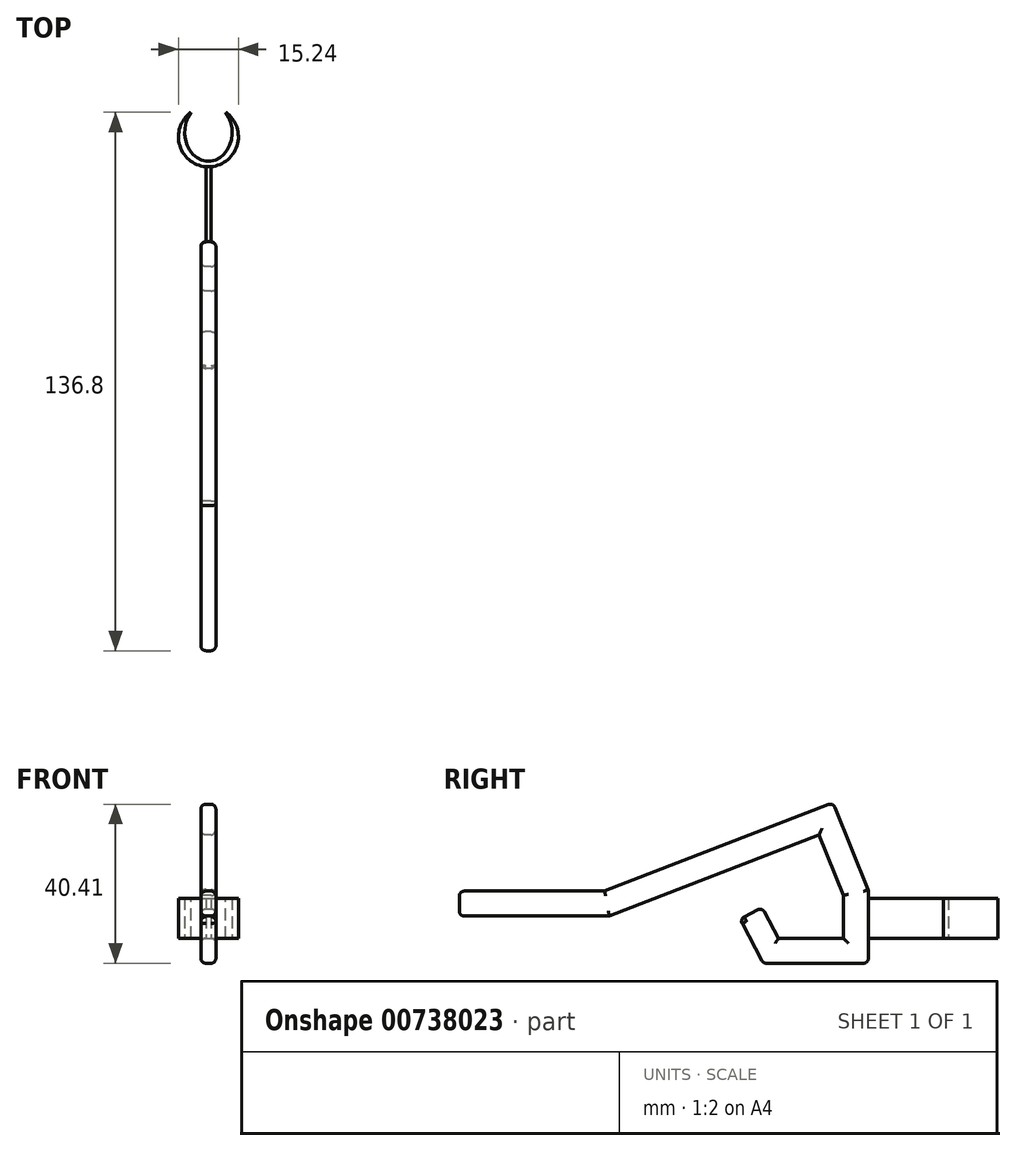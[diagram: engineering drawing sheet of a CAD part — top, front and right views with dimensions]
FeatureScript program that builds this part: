
annotation { "Feature Type Name" : "Feature", "Feature Type Description" : "" }
export const myFeature = defineFeature(function(context is Context, id is Id, definition is map)
    precondition{}
    {
        {
            var Q0;
            Q0=qCreatedBy(makeId("Right.planeOp"),FACE);
            var sketch = newSketch(context, id + "F0", { "sketchPlane" : qUnion([Q0])});
            skLineSegment(sketch, "E0", {"start": v(0, 0) * mm, "end": v(38.1, 0) * mm});
            skLineSegment(sketch, "E1", {"start": v(38.1, 0) * mm, "end": v(67.72, 11.44) * mm});
            skLineSegment(sketch, "E2", {"start": v(67.72, 11.44) * mm, "end": v(91.4, 20.6) * mm});
            skLineSegment(sketch, "E3", {"start": v(91.4, 20.6) * mm, "end": v(97.57, 5.28) * mm});
            skLineSegment(sketch, "E4", {"start": v(97.57, 5.28) * mm, "end": v(97.57, -5.65) * mm});
            skLineSegment(sketch, "E5", {"start": v(97.57, -5.65) * mm, "end": v(81.06, -5.65) * mm});
            skLineSegment(sketch, "E6", {"start": v(81.06, -5.65) * mm, "end": v(76.88, 2.2) * mm});
            skLineSegment(sketch, "E7", {"start": v(76.88, 2.2) * mm, "end": v(71.27, -0.8) * mm});
            skLineSegment(sketch, "E8", {"start": v(94.96, 28.78) * mm, "end": v(67.72, 18.25) * mm});
            skLineSegment(sketch, "E9", {"start": v(67.72, 18.25) * mm, "end": v(36.92, 6.35) * mm});
            skLineSegment(sketch, "E10", {"start": v(36.92, 6.35) * mm, "end": v(0, 6.35) * mm});
            skLineSegment(sketch, "E11", {"start": v(0, 6.35) * mm, "end": v(0, 0) * mm});
            skLineSegment(sketch, "E12", {"start": v(94.96, 28.78) * mm, "end": v(103.92, 6.5) * mm});
            skLineSegment(sketch, "E13", {"start": v(71.27, -0.8) * mm, "end": v(77.25, -12) * mm});
            skLineSegment(sketch, "E14", {"start": v(103.92, 6.5) * mm, "end": v(103.92, -12) * mm});
            skLineSegment(sketch, "E15", {"start": v(103.92, -12) * mm, "end": v(77.25, -12) * mm});
            skSolve(sketch);
        }
        {
            var Q0;
            Q0 = qSketchRegion(id + "F0", true);
            extrude(context, id + "F1", {"entities" : qUnion([Q0]), "depth" : 3.8 * mm, "offsetDistance" : 25.4 * mm});
        }
        {
            var Q0;
            Q0=makeQuery(id+"F1.opExtrude","SWEPT_EDGE",EDGE,{"disambiguationData":[OSD([sQuery(id+"F0.wireOp",EDGE,"E10"),sQuery(id+"F0.wireOp",EDGE,"E11")])]});
            var Q1;
            Q1=makeQuery(id+"F1.opExtrude","SWEPT_EDGE",EDGE,{"disambiguationData":[OSD([sQuery(id+"F0.wireOp",EDGE,"E0"),sQuery(id+"F0.wireOp",EDGE,"E11")])]});
            var Q2;
            Q2=makeQuery(id+"F1.opExtrude","CAP_EDGE",EDGE,{"disambiguationData":[OSD([sQuery(id+"F0.wireOp",EDGE,"E11")])],"isStart":false});
            var Q3;
            Q3=makeQuery(id+"F1.opExtrude","CAP_EDGE",EDGE,{"disambiguationData":[OSD([sQuery(id+"F0.wireOp",EDGE,"E0")])],"isStart":false});
            var Q4;
            Q4=makeQuery(id+"F1.opExtrude","CAP_EDGE",EDGE,{"disambiguationData":[OSD([sQuery(id+"F0.wireOp",EDGE,"E10")])],"isStart":false});
            var Q5;
            Q5=makeQuery(id+"F1.opExtrude","CAP_EDGE",EDGE,{"disambiguationData":[OSD([sQuery(id+"F0.wireOp",EDGE,"E0")])],"isStart":true});
            var Q6;
            Q6=makeQuery(id+"F1.opExtrude","CAP_EDGE",EDGE,{"disambiguationData":[OSD([sQuery(id+"F0.wireOp",EDGE,"E10")])],"isStart":true});
            var Q7;
            Q7=makeQuery(id+"F1.opExtrude","CAP_EDGE",EDGE,{"disambiguationData":[OSD([sQuery(id+"F0.wireOp",EDGE,"E9")])],"isStart":true});
            var Q8;
            Q8=makeQuery(id+"F1.opExtrude","CAP_EDGE",EDGE,{"disambiguationData":[OSD([sQuery(id+"F0.wireOp",EDGE,"E9")])],"isStart":false});
            var Q9;
            Q9=makeQuery(id+"F1.opExtrude","CAP_EDGE",EDGE,{"disambiguationData":[OSD([sQuery(id+"F0.wireOp",EDGE,"E1")])],"isStart":false});
            var Q10;
            Q10=makeQuery(id+"F1.opExtrude","CAP_EDGE",EDGE,{"disambiguationData":[OSD([sQuery(id+"F0.wireOp",EDGE,"E1")])],"isStart":true});
            var Q11;
            Q11=makeQuery(id+"F1.opExtrude","CAP_EDGE",EDGE,{"disambiguationData":[OSD([sQuery(id+"F0.wireOp",EDGE,"E11")])],"isStart":true});
            fillet(context, id + "F2", {"entities" : qUnion([Q0, Q1, Q2, Q3, Q4, Q5, Q6, Q7, Q8, Q9, Q10, Q11]), "radius" : 1.27 * mm, "tangentPropagation" : true, "allowEdgeOverflow" : false});
        }
        {
            var Q0;
            Q0=makeQuery(id+"F1.opExtrude","CAP_EDGE",EDGE,{"disambiguationData":[OSD([sQuery(id+"F0.wireOp",EDGE,"E8")])],"isStart":false});
            var Q1;
            Q1=makeQuery(id+"F1.opExtrude","CAP_EDGE",EDGE,{"disambiguationData":[OSD([sQuery(id+"F0.wireOp",EDGE,"E8")])],"isStart":true});
            var Q2;
            Q2=makeQuery(id+"F1.opExtrude","CAP_EDGE",EDGE,{"disambiguationData":[OSD([sQuery(id+"F0.wireOp",EDGE,"q7BT2R1Q-RqXa-ez77-BYZs-truSc1ktzAL2")])],"isStart":false});
            var Q3;
            Q3=makeQuery(id+"F1.opExtrude","CAP_EDGE",EDGE,{"disambiguationData":[OSD([sQuery(id+"F0.wireOp",EDGE,"q7BT2R1Q-RqXa-ez77-BYZs-truSc1ktzAL2")])],"isStart":true});
            var Q4;
            Q4=makeQuery(id+"F1.opExtrude","CAP_EDGE",EDGE,{"disambiguationData":[OSD([sQuery(id+"F0.wireOp",EDGE,"dIqGaWik-scwU-dTOI-6yUo-9ebBFIHKQPHa")])],"isStart":false});
            var Q5;
            Q5=makeQuery(id+"F1.opExtrude","CAP_EDGE",EDGE,{"disambiguationData":[OSD([sQuery(id+"F0.wireOp",EDGE,"dIqGaWik-scwU-dTOI-6yUo-9ebBFIHKQPHa")])],"isStart":true});
            var Q6;
            Q6=makeQuery(id+"F1.opExtrude","CAP_EDGE",EDGE,{"disambiguationData":[OSD([sQuery(id+"F0.wireOp",EDGE,"893hpDEh-NgwU-8noR-RPqz-osNGIVR5rFGW")])],"isStart":false});
            var Q7;
            Q7=makeQuery(id+"F1.opExtrude","CAP_EDGE",EDGE,{"disambiguationData":[OSD([sQuery(id+"F0.wireOp",EDGE,"893hpDEh-NgwU-8noR-RPqz-osNGIVR5rFGW")])],"isStart":true});
            var Q8;
            Q8=makeQuery(id+"F1.opExtrude","CAP_EDGE",EDGE,{"disambiguationData":[OSD([sQuery(id+"F0.wireOp",EDGE,"M6SEjoYa-NpJQ-ZD2F-zg5G-vaDSWslMFCXG")])],"isStart":false});
            var Q9;
            Q9=makeQuery(id+"F1.opExtrude","CAP_EDGE",EDGE,{"disambiguationData":[OSD([sQuery(id+"F0.wireOp",EDGE,"M6SEjoYa-NpJQ-ZD2F-zg5G-vaDSWslMFCXG")])],"isStart":true});
            var Q10;
            Q10=makeQuery(id+"F1.opExtrude","SWEPT_EDGE",EDGE,{"disambiguationData":[OSD([sQuery(id+"F0.wireOp",EDGE,"E7"),sQuery(id+"F0.wireOp",EDGE,"M6SEjoYa-NpJQ-ZD2F-zg5G-vaDSWslMFCXG")])]});
            var Q11;
            Q11=makeQuery(id+"F1.opExtrude","CAP_EDGE",EDGE,{"disambiguationData":[OSD([sQuery(id+"F0.wireOp",EDGE,"E7")])],"isStart":true});
            var Q12;
            Q12=makeQuery(id+"F1.opExtrude","CAP_EDGE",EDGE,{"disambiguationData":[OSD([sQuery(id+"F0.wireOp",EDGE,"E7")])],"isStart":false});
            var Q13;
            Q13=makeQuery(id+"F1.opExtrude","SWEPT_EDGE",EDGE,{"disambiguationData":[OSD([sQuery(id+"F0.wireOp",EDGE,"E6"),sQuery(id+"F0.wireOp",EDGE,"E7")])]});
            var Q14;
            Q14=makeQuery(id+"F1.opExtrude","CAP_EDGE",EDGE,{"disambiguationData":[OSD([sQuery(id+"F0.wireOp",EDGE,"E6")])],"isStart":false});
            var Q15;
            Q15=makeQuery(id+"F1.opExtrude","CAP_EDGE",EDGE,{"disambiguationData":[OSD([sQuery(id+"F0.wireOp",EDGE,"E6")])],"isStart":true});
            var Q16;
            Q16=makeQuery(id+"F1.opExtrude","CAP_EDGE",EDGE,{"disambiguationData":[OSD([sQuery(id+"F0.wireOp",EDGE,"E2")])],"isStart":true});
            var Q17;
            Q17=makeQuery(id+"F1.opExtrude","CAP_EDGE",EDGE,{"disambiguationData":[OSD([sQuery(id+"F0.wireOp",EDGE,"E2")])],"isStart":false});
            var Q18;
            Q18=makeQuery(id+"F1.opExtrude","CAP_EDGE",EDGE,{"disambiguationData":[OSD([sQuery(id+"F0.wireOp",EDGE,"E3")])],"isStart":true});
            var Q19;
            Q19=makeQuery(id+"F1.opExtrude","CAP_EDGE",EDGE,{"disambiguationData":[OSD([sQuery(id+"F0.wireOp",EDGE,"E3")])],"isStart":false});
            var Q20;
            Q20=makeQuery(id+"F1.opExtrude","CAP_EDGE",EDGE,{"disambiguationData":[OSD([sQuery(id+"F0.wireOp",EDGE,"E4")])],"isStart":true});
            var Q21;
            Q21=makeQuery(id+"F1.opExtrude","CAP_EDGE",EDGE,{"disambiguationData":[OSD([sQuery(id+"F0.wireOp",EDGE,"E4")])],"isStart":false});
            var Q22;
            Q22=makeQuery(id+"F1.opExtrude","CAP_EDGE",EDGE,{"disambiguationData":[OSD([sQuery(id+"F0.wireOp",EDGE,"E5")])],"isStart":true});
            var Q23;
            Q23=makeQuery(id+"F1.opExtrude","CAP_EDGE",EDGE,{"disambiguationData":[OSD([sQuery(id+"F0.wireOp",EDGE,"E5")])],"isStart":false});
            fillet(context, id + "F3", {"entities" : qUnion([Q0, Q1, Q2, Q3, Q4, Q5, Q6, Q7, Q8, Q9, Q10, Q11, Q12, Q13, Q14, Q15, Q16, Q17, Q18, Q19, Q20, Q21, Q22, Q23]), "radius" : 1.27 * mm, "tangentPropagation" : true, "allowEdgeOverflow" : false});
        }
        {
            var Q0;
            Q0=makeQuery(id+"F1.opExtrude","SWEPT_EDGE",EDGE,{"disambiguationData":[OSD([sQuery(id+"F0.wireOp",EDGE,"q7BT2R1Q-RqXa-ez77-BYZs-truSc1ktzAL2"),sQuery(id+"F0.wireOp",EDGE,"E8")])]});
            var Q1;
            Q1=makeQuery(id+"F1.opExtrude","SWEPT_EDGE",EDGE,{"disambiguationData":[OSD([sQuery(id+"F0.wireOp",EDGE,"893hpDEh-NgwU-8noR-RPqz-osNGIVR5rFGW"),sQuery(id+"F0.wireOp",EDGE,"dIqGaWik-scwU-dTOI-6yUo-9ebBFIHKQPHa")])]});
            var Q2;
            Q2=makeQuery(id+"F1.opExtrude","SWEPT_EDGE",EDGE,{"disambiguationData":[OSD([sQuery(id+"F0.wireOp",EDGE,"M6SEjoYa-NpJQ-ZD2F-zg5G-vaDSWslMFCXG"),sQuery(id+"F0.wireOp",EDGE,"893hpDEh-NgwU-8noR-RPqz-osNGIVR5rFGW")])]});
            fillet(context, id + "F4", {"entities" : qUnion([Q0, Q1, Q2]), "radius" : 1.27 * mm, "tangentPropagation" : true, "allowEdgeOverflow" : false});
        }
        {
            var Q0;
            Q0=makeQuery(id+"F1.opExtrude","CAP_EDGE",EDGE,{"disambiguationData":[OSD([sQuery(id+"F0.wireOp",EDGE,"E15")])],"isStart":true});
            var Q1;
            Q1=makeQuery(id+"F1.opExtrude","CAP_EDGE",EDGE,{"disambiguationData":[OSD([sQuery(id+"F0.wireOp",EDGE,"E15")])],"isStart":false});
            var Q2;
            Q2=makeQuery(id+"F1.opExtrude","SWEPT_EDGE",EDGE,{"disambiguationData":[OSD([sQuery(id+"F0.wireOp",EDGE,"E13"),sQuery(id+"F0.wireOp",EDGE,"E15")])]});
            var Q3;
            Q3=makeQuery(id+"F1.opExtrude","CAP_EDGE",EDGE,{"disambiguationData":[OSD([sQuery(id+"F0.wireOp",EDGE,"E13")])],"isStart":true});
            var Q4;
            Q4=makeQuery(id+"F1.opExtrude","CAP_EDGE",EDGE,{"disambiguationData":[OSD([sQuery(id+"F0.wireOp",EDGE,"E13")])],"isStart":false});
            var Q5;
            Q5=makeQuery(id+"F1.opExtrude","SWEPT_EDGE",EDGE,{"disambiguationData":[OSD([sQuery(id+"F0.wireOp",EDGE,"E14"),sQuery(id+"F0.wireOp",EDGE,"E15")])]});
            var Q6;
            Q6=makeQuery(id+"F1.opExtrude","SWEPT_EDGE",EDGE,{"disambiguationData":[OSD([sQuery(id+"F0.wireOp",EDGE,"E12"),sQuery(id+"F0.wireOp",EDGE,"E14")])]});
            fillet(context, id + "F5", {"entities" : qUnion([Q0, Q1, Q2, Q3, Q4, Q5, Q6]), "radius" : 1.27 * mm, "tangentPropagation" : true, "allowEdgeOverflow" : false});
        }
        {
            var Q0;
            Q0=makeQuery(id+"F1.opExtrude","SWEPT_FACE",FACE,{"disambiguationData":[OSD([sQuery(id+"F0.wireOp",EDGE,"E5")])]});
            var sketch = newSketch(context, id + "F6", { "sketchPlane" : qUnion([Q0])});
            skLineSegment(sketch, "E16.0", {"start": v(1.27, 103.92) * mm, "end": v(2.54, 103.92) * mm});
            skLineSegment(sketch, "E17", {"start": v(1.27, 103.92) * mm, "end": v(1.27, 122.97) * mm});
            skLineSegment(sketch, "E18", {"start": v(1.27, 122.97) * mm, "end": v(2.54, 122.97) * mm});
            skLineSegment(sketch, "E19", {"start": v(2.54, 122.97) * mm, "end": v(2.54, 103.92) * mm});
            skLineSegment(sketch, "E20", {"start": v(1.9, 122.97) * mm, "end": v(1.9, 130.59) * mm, "construction": true});
            skCircle(sketch, "E21", {"center": v(1.9, 130.59) * mm, "radius": 7.62 * mm});
            skSolve(sketch);
        }
        {
            var Q0;
            Q0 = qSketchRegion(id + "F6", true);
            extrude(context, id + "F7", {"entities" : qUnion([Q0]), "operationType" : NewBodyOperationType.ADD, "depth" : 10.16 * mm, "offsetDistance" : 25.4 * mm});
        }
        {
            var Q0;
            Q0=makeQuery(id+"F7.opExtrude","CAP_FACE",FACE,{"disambiguationData":[OSD([sQuery(id+"F6.wireOp",EDGE,"E21")])],"isStart":false});
            var sketch = newSketch(context, id + "F8", { "sketchPlane" : qUnion([Q0])});
            skCircle(sketch, "E22.0", {"center": v(1.9, 130.59) * mm, "radius": 7.62 * mm});
            skEllipse(sketch, "E23", {"center": v(1.9, 131.73) * mm, "majorRadius": 7.43 * mm, "minorRadius": 6.03 * mm, "majorAxis": v(0, -1)});
            skSolve(sketch);
        }
        {
            var Q0;
            {var subQ0=sQuery(id+"F8.wireOp",EDGE,"E23");var subQ1=sQuery(id+"F8.wireOp",EDGE,"E22.0");var subQ2=makeQuery(id+"F8.imprint","INTERSECT",VERTEX,{"disambiguationData":[OD(0.0)],"derivedFrom":[subQ1,subQ0]});Q0=makeQuery(id+"F8.imprint","IMPRINT",FACE,{"disambiguationData":[TD([[makeQuery(id+"F8.imprint","IMPRINT",EDGE,{"disambiguationData":[TD([[subQ2,1.0]])],"derivedFrom":subQ1}),1.0]])]});}
            var Q1;
            {var subQ0=sQuery(id+"F8.wireOp",EDGE,"E23");var subQ1=sQuery(id+"F8.wireOp",EDGE,"E22.0");var subQ2=makeQuery(id+"F8.imprint","INTERSECT",VERTEX,{"disambiguationData":[OD(0.0)],"derivedFrom":[subQ1,subQ0]});Q1=makeQuery(id+"F8.imprint","IMPRINT",FACE,{"disambiguationData":[TD([[makeQuery(id+"F8.imprint","IMPRINT",EDGE,{"disambiguationData":[TD([[subQ2,1.0]])],"derivedFrom":subQ1}),-1.0]])]});}
            extrude(context, id + "F9", {"entities" : qUnion([Q0, Q1]), "operationType" : NewBodyOperationType.REMOVE, "endBound" : BoundingType.THROUGH_ALL, "oppositeDirection" : true, "depth" : 25.4 * mm, "offsetDistance" : 25.4 * mm});
        }
    });
